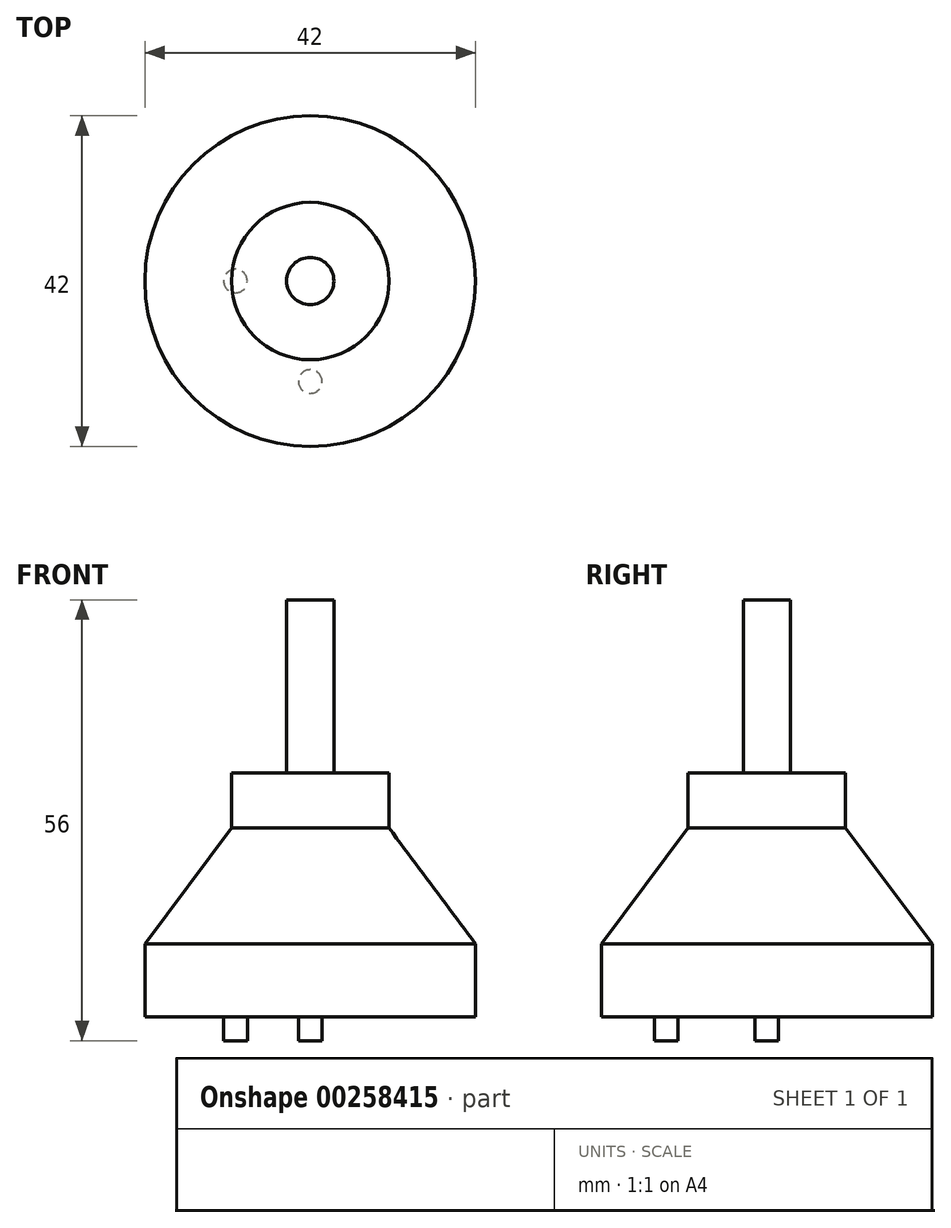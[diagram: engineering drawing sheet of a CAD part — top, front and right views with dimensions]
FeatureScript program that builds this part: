
annotation { "Feature Type Name" : "Feature", "Feature Type Description" : "" }
export const myFeature = defineFeature(function(context is Context, id is Id, definition is map)
    precondition{}
    {
        {
            var Q0;
            Q0=qCreatedBy(makeId("Front.planeOp"),FACE);
            var sketch = newSketch(context, id + "F0", { "sketchPlane" : qUnion([Q0])});
            skLineSegment(sketch, "E0.bottom", {"start": v(0, -6.15) * mm, "end": v(21, -6.15) * mm});
            skLineSegment(sketch, "E0.right", {"start": v(21, -6.15) * mm, "end": v(21, 6.15) * mm});
            skLineSegment(sketch, "E1.top", {"start": v(0, 49.85) * mm, "end": v(3, 49.85) * mm});
            skLineSegment(sketch, "E2.bottom", {"start": v(3, 27.85) * mm, "end": v(10, 27.85) * mm});
            skLineSegment(sketch, "E2.right", {"start": v(10, 27.85) * mm, "end": v(10, 20.85) * mm});
            skLineSegment(sketch, "E3", {"start": v(10, 20.85) * mm, "end": v(21, 6.15) * mm});
            skLineSegment(sketch, "E4.trimOffspring", {"start": v(3, 27.85) * mm, "end": v(3, 49.85) * mm});
            skPoint(sketch, "E2.left.start.orphan", {"position": v(0, 27.85) * mm});
            skLineSegment(sketch, "E5", {"start": v(0, -6.15) * mm, "end": v(0, 49.85) * mm});
            skLineSegment(sketch, "E6", {"start": v(0, 63.2) * mm, "end": v(0, -21.26) * mm, "construction": true});
            skSolve(sketch);
        }
        {
            var Q0;
            Q0=makeQuery(id+"F0.imprint","IMPRINT",FACE,{"disambiguationData":[TD([[makeQuery(id+"F0.imprint","IMPRINT",EDGE,{"derivedFrom":sQuery(id+"F0.wireOp",EDGE,"E0.bottom")}),1.0]])]});
            var Q1;
            Q1=sQuery(id+"F0.wireOp",EDGE,"E6");
            revolve(context, id + "F1", {"entities" : qUnion([Q0]), "axis" : qUnion([Q1]), "revolveType" : RevolveType.FULL});
        }
        {
            var Q0;
            Q0=makeQuery(id+"F1.opRevolve","SWEPT_FACE",FACE,{"disambiguationData":[OSD([sQuery(id+"F0.wireOp",EDGE,"E0.bottom")])]});
            var sketch = newSketch(context, id + "F2", { "sketchPlane" : qUnion([Q0])});
            skCircle(sketch, "E7", {"center": v(0, 0) * mm, "radius": 5.25 * mm});
            skCircle(sketch, "E8", {"center": v(0, -12.77) * mm, "radius": 1.5 * mm});
            skCircle(sketch, "E9.MirrorC", {"center": v(0, 12.77) * mm, "radius": 1.5 * mm});
            skCircle(sketch, "E10", {"center": v(9.5, 0) * mm, "radius": 1.5 * mm});
            skCircle(sketch, "E11.MirrorC", {"center": v(-9.5, 0) * mm, "radius": 1.5 * mm});
            skSolve(sketch);
        }
        {
            var Q0;
            Q0=makeQuery(id+"F2.imprint","IMPRINT",FACE,{"disambiguationData":[TD([[makeQuery(id+"F2.imprint","IMPRINT",EDGE,{"derivedFrom":sQuery(id+"F2.wireOp",EDGE,"E7")}),1.0]])]});
            var Q1;
            Q1=makeQuery(id+"F2.imprint","IMPRINT",FACE,{"disambiguationData":[TD([[makeQuery(id+"F2.imprint","IMPRINT",EDGE,{"derivedFrom":sQuery(id+"F2.wireOp",EDGE,"E8")}),1.0]])]});
            var Q2;
            Q2=makeQuery(id+"F2.imprint","IMPRINT",FACE,{"disambiguationData":[TD([[makeQuery(id+"F2.imprint","IMPRINT",EDGE,{"derivedFrom":sQuery(id+"F2.wireOp",EDGE,"E10")}),1.0]])]});
            var Q3;
            Q3=makeQuery(id+"F2.imprint","IMPRINT",FACE,{"disambiguationData":[TD([[makeQuery(id+"F2.imprint","IMPRINT",EDGE,{"derivedFrom":sQuery(id+"F2.wireOp",EDGE,"E11.MirrorC")}),-1.0]])]});
            var Q4;
            Q4=makeQuery(id+"F2.imprint","IMPRINT",FACE,{"disambiguationData":[TD([[makeQuery(id+"F2.imprint","IMPRINT",EDGE,{"derivedFrom":sQuery(id+"F2.wireOp",EDGE,"E9.MirrorC")}),-1.0]])]});
            extrude(context, id + "F3", {"entities" : qUnion([Q0, Q1, Q2, Q3, Q4]), "operationType" : NewBodyOperationType.REMOVE, "oppositeDirection" : true, "depth" : 3 * mm});
        }
    });
